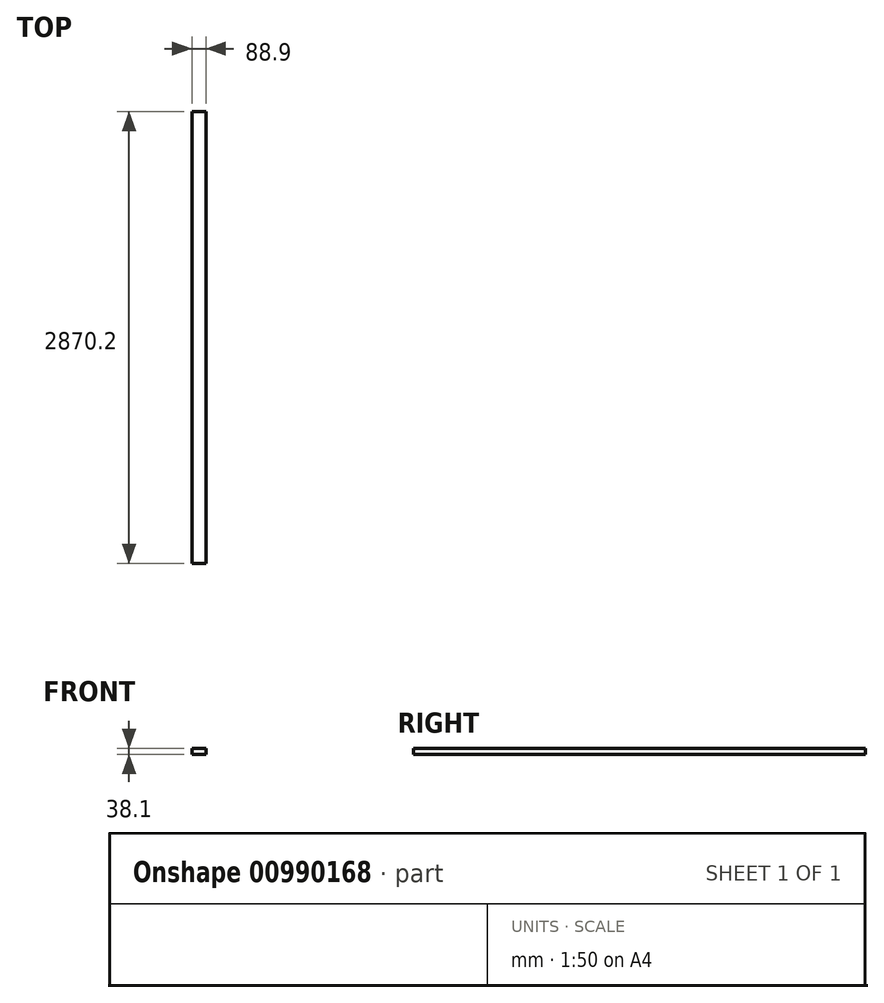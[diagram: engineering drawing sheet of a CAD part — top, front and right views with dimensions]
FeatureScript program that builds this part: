
annotation { "Feature Type Name" : "Feature", "Feature Type Description" : "" }
export const myFeature = defineFeature(function(context is Context, id is Id, definition is map)
    precondition{}
    {
        {
            assignVariable(context, id + "F0", {"name" : "w", "anyValue" : 38.1 * mm});
        }
        {
            var Q0;
            Q0=qCreatedBy(makeId("Top.planeOp"),FACE);
            var sketch = newSketch(context, id + "F1", { "sketchPlane" : qUnion([Q0])});
            skLineSegment(sketch, "E0.bottom", {"start": v(44.45, 1435.1) * mm, "end": v(-44.45, 1435.1) * mm});
            skLineSegment(sketch, "E0.top", {"start": v(44.45, -1435.1) * mm, "end": v(-44.45, -1435.1) * mm});
            skLineSegment(sketch, "E0.left", {"start": v(44.45, 1435.1) * mm, "end": v(44.45, -1435.1) * mm});
            skLineSegment(sketch, "E0.right", {"start": v(-44.45, 1435.1) * mm, "end": v(-44.45, -1435.1) * mm});
            skPoint(sketch, "E0.middle", {"position": v(0, 0) * mm});
            skSolve(sketch);
        }
        {
            var Q0;
            Q0=qSketchRegion(id+"F1",true);
            extrude(context, id + "F2", {"entities" : qUnion([Q0]), "depth" : getVariable(context, 'w'), "offsetDistance" : 25.4 * mm});
        }
    });
